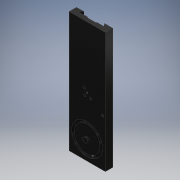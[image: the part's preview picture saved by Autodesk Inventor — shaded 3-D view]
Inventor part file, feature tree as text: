
AUTODESK INVENTOR PART (.ipt)
format: ipt  version: 2018 (Build 220112000, 112)  size: 252,416 bytes
history: native  units: mm
features: extrude x9, sketch x8, hole x4, thread x3, fillet x1
ambient origin geometry x8: Origin, YZ Plane, XZ Plane, XY Plane, X Axis, Y Axis, Z Axis, Center Point
bodies: Solid1 (feature_tree)
feature tree (25):
  extrude  "Extrusion1"  Depth=29.6mm
  sketch  "Sketch2"  dims[d2=29.9mm d4=22.68928mm]
  sketch  "Sketch3"  dims[d5=33.0mm d6=8.726646mm]
  extrude  "Extrusion2"  Depth=29.9mm
  extrude  "Extrusion3"  Depth=33.0mm
  extrude  "Extrusion4"  Depth=486.0mm
  sketch  "Sketch4"  dims[d7=486.0mm d8=0.0mm d9=22.0mm]
  extrude  "Extrusion5"  Depth=14.5mm
  extrude  "Extrusion7"  Depth=62.1mm
  extrude  "Extrusion8"  Depth=8.2mm
  sketch  "Sketch5"  dims[d10=124.2mm d11=14.5mm]
  hole  "Hole1"  [1 undecoded]
  hole  "Hole2"  [1 undecoded]
  hole  "Hole3"  [1 undecoded]
  thread  "Thread1"  [1 undecoded]
  extrude  "Extrusion11"  Depth=9.4mm
  extrude  "Extrusion13"  TaperAngle=0.0deg  [1 undecoded]
  hole  "Hole5"  [1 undecoded]
  thread  "Thread6"  [1 undecoded]
  thread  "Thread7"  [1 undecoded]
  fillet  "Fillet1"  Radius=17.0mm
  sketch  "Sketch1"  dims[d0=146.0mm d1=29.6mm]
  sketch  "Sketch14"  dims[d12=62.1mm d13=104.0mm]
  sketch  "Sketch17"  dims[d14=19.02mm d15=8.2mm]
  sketch  "Sketch18"  dims[d17=13.0mm d18=0.0mm d19=7.5mm d20=0.0mm d21=7.5mm d22=0.0mm d23=19.0mm d24=3.7mm d25=0.0mm d26=9.4mm d29=0.0mm d30=18.7mm d31=18.7mm d36=6.0mm d37=0.0mm d38=17.0mm d39=46.5mm d40=3.0mm d41=0.0mm d45=11.0mm d46=60.5mm d47=250.5mm d48=11.0mm d49=190.5mm d50=11.5mm d51=8.5mm d52=6.0mm d53=11.0mm d54=8.5mm d55=90.0deg d56=8.0mm d57=20.594885mm d58=7.0mm d59=0.599mm d60=10.0mm d61=7.5mm d62=90.0deg d63=8.0mm d64=20.594885mm d65=7.5mm d66=6.0mm d67=11.0mm d68=7.0mm d69=90.0deg d70=8.0mm d71=20.594885mm d75=10.0mm d76=0.0mm d82=39.0mm d83=83.1mm d84=64.0mm d85=6.0mm d86=0.0mm d99=19.35mm d100=38.0mm d101=145.0mm d102=3.0mm d103=0.0mm d112=22.7mm d113=7.0mm d114=6.0mm d115=10.0mm d116=7.5mm d117=90.0deg d118=8.0mm d119=20.594885mm d120=10.0mm d121=0.0mm d122=10.0mm d123=0.0mm d124=10.0mm]
note: 8 required parameter values undecoded (feature->parameter linkage not recoverable at this tier; creation-order binding heuristic only, values carry confidence <= 0.55)
